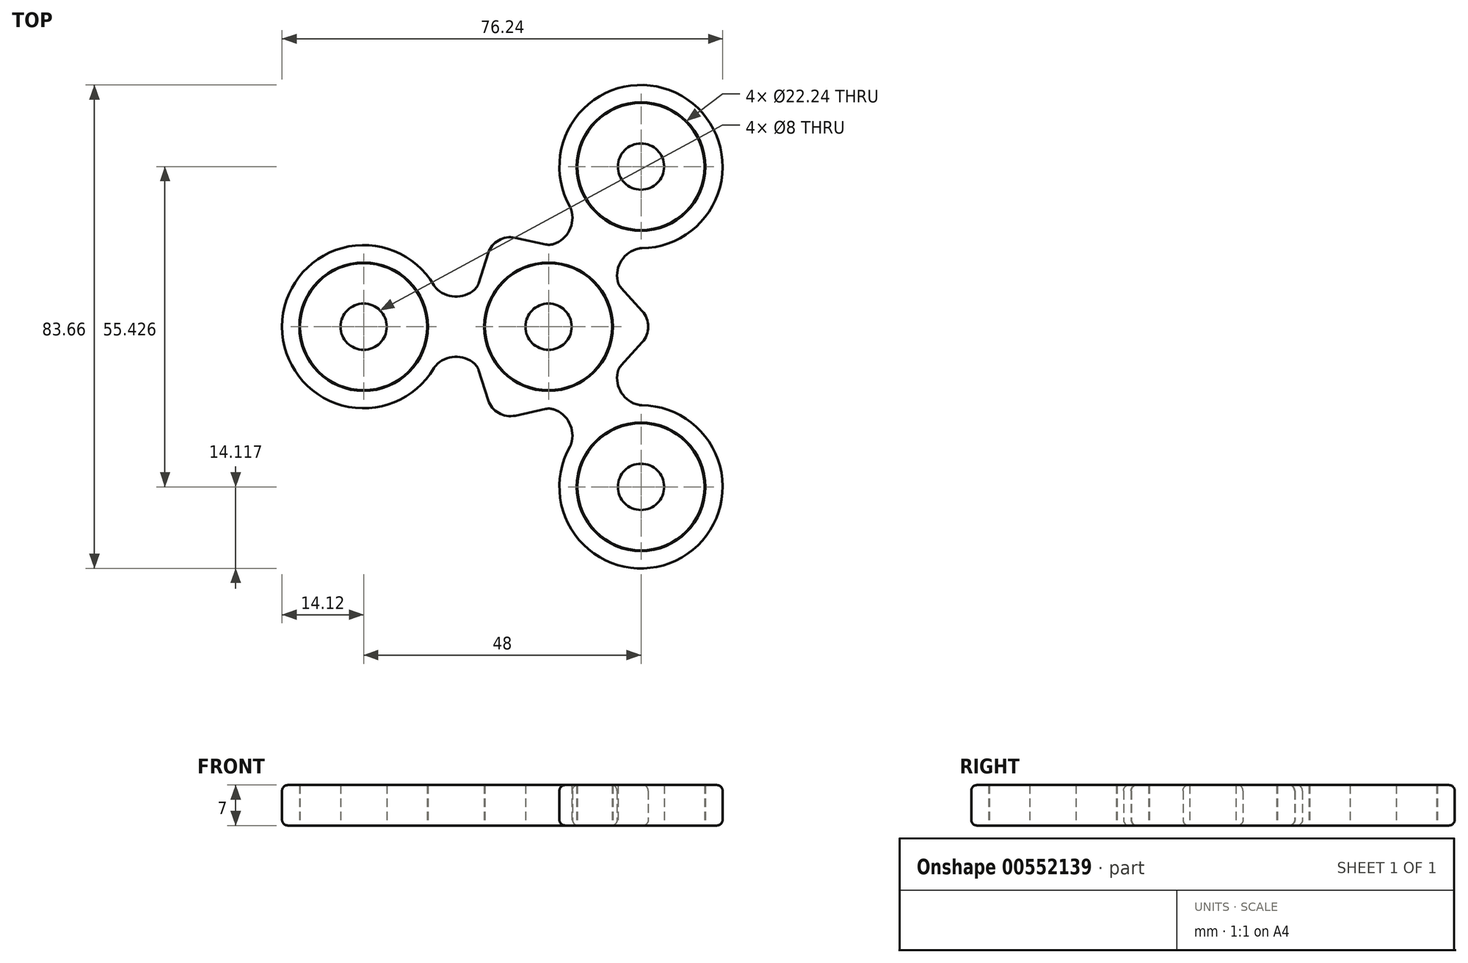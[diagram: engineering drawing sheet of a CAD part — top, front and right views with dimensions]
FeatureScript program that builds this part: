
annotation { "Feature Type Name" : "Feature", "Feature Type Description" : "" }
export const myFeature = defineFeature(function(context is Context, id is Id, definition is map)
    precondition{}
    {
        {
            var Q0;
            Q0=qCreatedBy(makeId("Top.planeOp"),FACE);
            var sketch = newSketch(context, id + "F0", { "sketchPlane" : qUnion([Q0])});
            skCircle(sketch, "E0", {"center": v(0, 0) * mm, "radius": 11 * mm});
            skCircle(sketch, "E1", {"center": v(0, 0) * mm, "radius": 4 * mm});
            skSolve(sketch);
        }
        {
            var Q0;
            Q0=makeQuery(id+"F0.imprint","IMPRINT",FACE,{"disambiguationData":[TD([[makeQuery(id+"F0.imprint","IMPRINT",EDGE,{"derivedFrom":sQuery(id+"F0.wireOp",EDGE,"E0")}),1.0]])]});
            extrude(context, id + "F1", {"entities" : qUnion([Q0]), "endBound" : BoundingType.SYMMETRIC, "depth" : 7 * mm, "offsetDistance" : 25.4 * mm});
        }
        {
            var Q0;
            Q0=qCreatedBy(makeId("Top.planeOp"),FACE);
            var sketch = newSketch(context, id + "F2", { "sketchPlane" : qUnion([Q0])});
            skCircle(sketch, "E2", {"center": v(-32, 0) * mm, "radius": 11 * mm});
            skCircle(sketch, "E3", {"center": v(-32, 0) * mm, "radius": 4 * mm});
            skCircle(sketch, "E4.1.0", {"center": v(16, -27.71) * mm, "radius": 11 * mm});
            skCircle(sketch, "E4.1.1", {"center": v(16, -27.71) * mm, "radius": 4 * mm});
            skCircle(sketch, "E4.2.0", {"center": v(16, 27.71) * mm, "radius": 11 * mm});
            skCircle(sketch, "E4.2.1", {"center": v(16, 27.71) * mm, "radius": 4 * mm});
            skPoint(sketch, "E4.center", {"position": v(0, 0) * mm});
            skSolve(sketch);
        }
        {
            var Q0;
            Q0=makeQuery(id+"F2.imprint","IMPRINT",FACE,{"disambiguationData":[TD([[makeQuery(id+"F2.imprint","IMPRINT",EDGE,{"derivedFrom":sQuery(id+"F2.wireOp",EDGE,"E2")}),1.0]])]});
            var Q1;
            Q1=makeQuery(id+"F2.imprint","IMPRINT",FACE,{"disambiguationData":[TD([[makeQuery(id+"F2.imprint","IMPRINT",EDGE,{"derivedFrom":sQuery(id+"F2.wireOp",EDGE,"E4.2.0")}),1.0]])]});
            var Q2;
            Q2=makeQuery(id+"F2.imprint","IMPRINT",FACE,{"disambiguationData":[TD([[makeQuery(id+"F2.imprint","IMPRINT",EDGE,{"derivedFrom":sQuery(id+"F2.wireOp",EDGE,"E4.1.0")}),1.0]])]});
            extrude(context, id + "F3", {"entities" : qUnion([Q0, Q1, Q2]), "endBound" : BoundingType.SYMMETRIC, "depth" : 7 * mm, "offsetDistance" : 25 * mm});
        }
        {
            var Q0;
            Q0=qCreatedBy(makeId("Top.planeOp"),FACE);
            var sketch = newSketch(context, id + "F4", { "sketchPlane" : qUnion([Q0])});
            skCircle(sketch, "E5.0", {"center": v(-32, 0) * mm, "radius": 11.12 * mm});
            skCircle(sketch, "E6.0", {"center": v(-32, 0) * mm, "radius": 14.12 * mm});
            skPoint(sketch, "E7.center", {"position": v(0, 0) * mm});
            skCircle(sketch, "E8", {"center": v(0, 0) * mm, "radius": 14.12 * mm});
            skCircle(sketch, "E9", {"center": v(0, 0) * mm, "radius": 11.12 * mm});
            skLineSegment(sketch, "E10", {"start": v(-12.26, -7) * mm, "end": v(-10.44, -12.7) * mm});
            skLineSegment(sketch, "E11", {"start": v(-5.78, -15.4) * mm, "end": v(0.07, -14.12) * mm});
            skPoint(sketch, "E12.visualSharp", {"position": v(-9.33, -16.17) * mm});
            skArc(sketch, "E12.filletArc", {"start": v(-10.44, -12.7) * mm, "mid": v(-8.63, -14.95) * mm, "end": v(-5.78, -15.4) * mm});
            skLineSegment(sketch, "E13.1.0", {"start": v(12.2, -7.12) * mm, "end": v(16.22, -2.7) * mm});
            skArc(sketch, "E13.1.1", {"start": v(16.22, -2.7) * mm, "mid": v(17.26, 0) * mm, "end": v(16.22, 2.7) * mm});
            skLineSegment(sketch, "E13.1.2", {"start": v(16.22, 2.7) * mm, "end": v(12.2, 7.12) * mm});
            skLineSegment(sketch, "E13.2.0", {"start": v(0.07, 14.12) * mm, "end": v(-5.78, 15.4) * mm});
            skArc(sketch, "E13.2.1", {"start": v(-5.78, 15.4) * mm, "mid": v(-8.63, 14.95) * mm, "end": v(-10.44, 12.7) * mm});
            skLineSegment(sketch, "E13.2.2", {"start": v(-10.44, 12.7) * mm, "end": v(-12.26, 7) * mm});
            skLineSegment(sketch, "E14", {"start": v(-32, 0) * mm, "end": v(0, 0) * mm, "construction": true});
            skArc(sketch, "E15", {"start": v(-19.74, 7) * mm, "mid": v(-16, 5.2) * mm, "end": v(-12.26, 7) * mm});
            skArc(sketch, "E16.MirrorCS", {"start": v(-19.74, -7) * mm, "mid": v(-16, -5.2) * mm, "end": v(-12.26, -7) * mm});
            skArc(sketch, "E17.1.0", {"start": v(3.8, -20.6) * mm, "mid": v(3.5, -16.46) * mm, "end": v(0.07, -14.12) * mm});
            skCircle(sketch, "E17.1.1", {"center": v(16, -27.71) * mm, "radius": 14.12 * mm});
            skCircle(sketch, "E17.1.2", {"center": v(16, -27.71) * mm, "radius": 11.12 * mm});
            skArc(sketch, "E17.1.3", {"start": v(15.93, -13.6) * mm, "mid": v(12.5, -11.26) * mm, "end": v(12.2, -7.12) * mm});
            skLineSegment(sketch, "E17.1.4", {"start": v(16, -27.71) * mm, "end": v(0, 0) * mm, "construction": true});
            skArc(sketch, "E17.2.0", {"start": v(15.93, 13.6) * mm, "mid": v(12.5, 11.26) * mm, "end": v(12.2, 7.12) * mm});
            skCircle(sketch, "E17.2.1", {"center": v(16, 27.71) * mm, "radius": 14.12 * mm});
            skCircle(sketch, "E17.2.2", {"center": v(16, 27.71) * mm, "radius": 11.12 * mm});
            skArc(sketch, "E17.2.3", {"start": v(3.8, 20.6) * mm, "mid": v(3.5, 16.46) * mm, "end": v(0.07, 14.12) * mm});
            skLineSegment(sketch, "E17.2.4", {"start": v(16, 27.71) * mm, "end": v(0, 0) * mm, "construction": true});
            skSolve(sketch);
        }
        {
            var Q0;
            Q0=makeQuery(id+"F4.imprint","IMPRINT",FACE,{"disambiguationData":[TD([[makeQuery(id+"F4.imprint","IMPRINT",EDGE,{"derivedFrom":sQuery(id+"F4.wireOp",EDGE,"E5.0")}),-1.0]])]});
            var Q1;
            {var subQ0=sQuery(id+"F4.wireOp",EDGE,"gArRicI1-MkRc-wUEB-PXOf-4bWENSXwJS3J");Q1=makeQuery(id+"F4.imprint","IMPRINT",FACE,{"disambiguationData":[TD([[makeQuery(id+"F4.imprint","IMPRINT",EDGE,{"derivedFrom":subQ0}),-1.0]])]});}
            var Q2;
            {var subQ0=sQuery(id+"F4.wireOp",EDGE,"E7.2.2");Q2=makeQuery(id+"F4.imprint","IMPRINT",FACE,{"disambiguationData":[TD([[makeQuery(id+"F4.imprint","IMPRINT",EDGE,{"derivedFrom":subQ0}),-1.0]])]});}
            var Q3;
            Q3=makeQuery(id+"F4.imprint","IMPRINT",FACE,{"disambiguationData":[TD([[makeQuery(id+"F4.imprint","IMPRINT",EDGE,{"derivedFrom":sQuery(id+"F4.wireOp",EDGE,"E7.2.1")}),-1.0]])]});
            var Q4;
            {var subQ0=sQuery(id+"F4.wireOp",EDGE,"E7.1.2");Q4=makeQuery(id+"F4.imprint","IMPRINT",FACE,{"disambiguationData":[TD([[makeQuery(id+"F4.imprint","IMPRINT",EDGE,{"derivedFrom":subQ0}),-1.0]])]});}
            var Q5;
            Q5=makeQuery(id+"F4.imprint","IMPRINT",FACE,{"disambiguationData":[TD([[makeQuery(id+"F4.imprint","IMPRINT",EDGE,{"derivedFrom":sQuery(id+"F4.wireOp",EDGE,"E7.1.1")}),-1.0]])]});
            var Q6;
            Q6=makeQuery(id+"F4.imprint","IMPRINT",FACE,{"disambiguationData":[TD([[makeQuery(id+"F4.imprint","IMPRINT",EDGE,{"derivedFrom":sQuery(id+"F4.wireOp",EDGE,"T5eTbelr-j5SR-9AlQ-x1VE-5ucUHFY7ANY2")}),-1.0]])]});
            var Q7;
            Q7=makeQuery(id+"F4.imprint","IMPRINT",FACE,{"disambiguationData":[TD([[makeQuery(id+"F4.imprint","IMPRINT",EDGE,{"derivedFrom":sQuery(id+"F4.wireOp",EDGE,"E9")}),-1.0]])]});
            var Q8;
            {var subQ0=sQuery(id+"F4.wireOp",EDGE,"E8");var subQ1=sQuery(id+"F4.wireOp",EDGE,"E7.2.0");var subQ2=makeQuery(id+"F4.imprint","INTERSECT",VERTEX,{"disambiguationData":[OD(0.0)],"derivedFrom":[subQ1,subQ0]});Q8=makeQuery(id+"F4.imprint","IMPRINT",FACE,{"disambiguationData":[TD([[makeQuery(id+"F4.imprint","IMPRINT",EDGE,{"disambiguationData":[TD([[subQ2,1.0]])],"derivedFrom":subQ1}),1.0]])]});}
            var Q9;
            {var subQ0=sQuery(id+"F4.wireOp",EDGE,"E7.2.4");Q9=makeQuery(id+"F4.imprint","IMPRINT",FACE,{"disambiguationData":[TD([[makeQuery(id+"F4.imprint","IMPRINT",EDGE,{"derivedFrom":subQ0}),1.0]])]});}
            var Q10;
            {var subQ0=sQuery(id+"F4.wireOp",EDGE,"E8");var subQ1=sQuery(id+"F4.wireOp",EDGE,"E6.0");var subQ2=makeQuery(id+"F4.imprint","INTERSECT",VERTEX,{"disambiguationData":[OD(0.0)],"derivedFrom":[subQ1,subQ0]});Q10=makeQuery(id+"F4.imprint","IMPRINT",FACE,{"disambiguationData":[TD([[makeQuery(id+"F4.imprint","IMPRINT",EDGE,{"disambiguationData":[TD([[subQ2,1.0]])],"derivedFrom":subQ1}),1.0]])]});}
            var Q11;
            {var subQ0=sQuery(id+"F4.wireOp",EDGE,"8a5024f6-34da-4b4a-a497-6fec5d8cf57b0.MirrorCS");Q11=makeQuery(id+"F4.imprint","IMPRINT",FACE,{"disambiguationData":[TD([[makeQuery(id+"F4.imprint","IMPRINT",EDGE,{"derivedFrom":subQ0}),1.0]])]});}
            var Q12;
            {var subQ0=sQuery(id+"F4.wireOp",EDGE,"E8");var subQ1=sQuery(id+"F4.wireOp",EDGE,"E7.1.0");var subQ2=makeQuery(id+"F4.imprint","INTERSECT",VERTEX,{"disambiguationData":[OD(0.0)],"derivedFrom":[subQ1,subQ0]});Q12=makeQuery(id+"F4.imprint","IMPRINT",FACE,{"disambiguationData":[TD([[makeQuery(id+"F4.imprint","IMPRINT",EDGE,{"disambiguationData":[TD([[subQ2,1.0]])],"derivedFrom":subQ1}),1.0]])]});}
            var Q13;
            {var subQ0=sQuery(id+"F4.wireOp",EDGE,"E7.1.4");Q13=makeQuery(id+"F4.imprint","IMPRINT",FACE,{"disambiguationData":[TD([[makeQuery(id+"F4.imprint","IMPRINT",EDGE,{"derivedFrom":subQ0}),1.0]])]});}
            var Q14;
            {var subQ2=sQuery(id+"F4.wireOp",EDGE,"E13.2.0");Q14=makeQuery(id+"F4.imprint","IMPRINT",FACE,{"disambiguationData":[TD([[makeQuery(id+"F4.imprint","IMPRINT",EDGE,{"derivedFrom":subQ2}),1.0]])]});}
            var Q15;
            {var subQ0=sQuery(id+"F4.wireOp",EDGE,"E10");Q15=makeQuery(id+"F4.imprint","IMPRINT",FACE,{"disambiguationData":[TD([[makeQuery(id+"F4.imprint","IMPRINT",EDGE,{"derivedFrom":subQ0}),1.0]])]});}
            var Q16;
            {var subQ0=sQuery(id+"F4.wireOp",EDGE,"E13.1.0");Q16=makeQuery(id+"F4.imprint","IMPRINT",FACE,{"disambiguationData":[TD([[makeQuery(id+"F4.imprint","IMPRINT",EDGE,{"derivedFrom":subQ0}),1.0]])]});}
            var Q17;
            {var subQ0=sQuery(id+"F4.wireOp",EDGE,"E15");Q17=makeQuery(id+"F4.imprint","IMPRINT",FACE,{"disambiguationData":[TD([[makeQuery(id+"F4.imprint","IMPRINT",EDGE,{"derivedFrom":subQ0}),-1.0]])]});}
            var Q18;
            {var subQ0=sQuery(id+"F4.wireOp",EDGE,"E17.2.0");Q18=makeQuery(id+"F4.imprint","IMPRINT",FACE,{"disambiguationData":[TD([[makeQuery(id+"F4.imprint","IMPRINT",EDGE,{"derivedFrom":subQ0}),-1.0]])]});}
            var Q19;
            Q19=makeQuery(id+"F4.imprint","IMPRINT",FACE,{"disambiguationData":[TD([[makeQuery(id+"F4.imprint","IMPRINT",EDGE,{"derivedFrom":sQuery(id+"F4.wireOp",EDGE,"E17.2.2")}),-1.0]])]});
            var Q20;
            {var subQ0=sQuery(id+"F4.wireOp",EDGE,"E17.1.0");Q20=makeQuery(id+"F4.imprint","IMPRINT",FACE,{"disambiguationData":[TD([[makeQuery(id+"F4.imprint","IMPRINT",EDGE,{"derivedFrom":subQ0}),-1.0]])]});}
            var Q21;
            Q21=makeQuery(id+"F4.imprint","IMPRINT",FACE,{"disambiguationData":[TD([[makeQuery(id+"F4.imprint","IMPRINT",EDGE,{"derivedFrom":sQuery(id+"F4.wireOp",EDGE,"E17.1.2")}),-1.0]])]});
            extrude(context, id + "F5", {"entities" : qUnion([Q0, Q1, Q2, Q3, Q4, Q5, Q6, Q7, Q8, Q9, Q10, Q11, Q12, Q13, Q14, Q15, Q16, Q17, Q18, Q19, Q20, Q21]), "endBound" : BoundingType.SYMMETRIC, "depth" : 7 * mm, "offsetDistance" : 25 * mm});
        }
        {
            var Q0;
            Q0=makeQuery(id+"F5.opExtrude","SWEPT_EDGE",EDGE,{"disambiguationData":[OSD([sQuery(id+"F4.wireOp",EDGE,"E7.2.0"),sQuery(id+"F4.wireOp",EDGE,"E7.2.2")])]});
            var Q1;
            Q1=makeQuery(id+"F5.opExtrude","SWEPT_EDGE",EDGE,{"disambiguationData":[OSD([sQuery(id+"F4.wireOp",EDGE,"E7.2.2"),sQuery(id+"F4.wireOp",EDGE,"E8")])]});
            var Q2;
            Q2=makeQuery(id+"F5.opExtrude","SWEPT_EDGE",EDGE,{"disambiguationData":[OSD([sQuery(id+"F4.wireOp",EDGE,"E7.1.4"),sQuery(id+"F4.wireOp",EDGE,"E8")])]});
            var Q3;
            Q3=makeQuery(id+"F5.opExtrude","SWEPT_EDGE",EDGE,{"disambiguationData":[OSD([sQuery(id+"F4.wireOp",EDGE,"E7.1.0"),sQuery(id+"F4.wireOp",EDGE,"E7.1.4")])]});
            var Q4;
            Q4=makeQuery(id+"F5.opExtrude","SWEPT_EDGE",EDGE,{"disambiguationData":[OSD([sQuery(id+"F4.wireOp",EDGE,"E7.2.4"),sQuery(id+"F4.wireOp",EDGE,"E8")])]});
            var Q5;
            Q5=makeQuery(id+"F5.opExtrude","SWEPT_EDGE",EDGE,{"disambiguationData":[OSD([sQuery(id+"F4.wireOp",EDGE,"E7.2.0"),sQuery(id+"F4.wireOp",EDGE,"E7.2.4")])]});
            var Q6;
            Q6=makeQuery(id+"F5.opExtrude","SWEPT_EDGE",EDGE,{"disambiguationData":[OSD([sQuery(id+"F4.wireOp",EDGE,"gArRicI1-MkRc-wUEB-PXOf-4bWENSXwJS3J"),sQuery(id+"F4.wireOp",EDGE,"E8")])]});
            var Q7;
            Q7=makeQuery(id+"F5.opExtrude","SWEPT_EDGE",EDGE,{"disambiguationData":[OSD([sQuery(id+"F4.wireOp",EDGE,"E6.0"),sQuery(id+"F4.wireOp",EDGE,"gArRicI1-MkRc-wUEB-PXOf-4bWENSXwJS3J")])]});
            var Q8;
            Q8=makeQuery(id+"F5.opExtrude","SWEPT_EDGE",EDGE,{"disambiguationData":[OSD([sQuery(id+"F4.wireOp",EDGE,"E6.0"),sQuery(id+"F4.wireOp",EDGE,"8a5024f6-34da-4b4a-a497-6fec5d8cf57b0.MirrorCS")])]});
            var Q9;
            Q9=makeQuery(id+"F5.opExtrude","SWEPT_EDGE",EDGE,{"disambiguationData":[OSD([sQuery(id+"F4.wireOp",EDGE,"8a5024f6-34da-4b4a-a497-6fec5d8cf57b0.MirrorCS"),sQuery(id+"F4.wireOp",EDGE,"E8")])]});
            var Q10;
            Q10=makeQuery(id+"F5.opExtrude","SWEPT_EDGE",EDGE,{"disambiguationData":[OSD([sQuery(id+"F4.wireOp",EDGE,"E7.1.2"),sQuery(id+"F4.wireOp",EDGE,"E8")])]});
            var Q11;
            Q11=makeQuery(id+"F5.opExtrude","SWEPT_EDGE",EDGE,{"disambiguationData":[OSD([sQuery(id+"F4.wireOp",EDGE,"E7.1.0"),sQuery(id+"F4.wireOp",EDGE,"E7.1.2")])]});
            var Q12;
            Q12=makeQuery(id+"F5.opExtrude","SWEPT_EDGE",EDGE,{"disambiguationData":[OSD([sQuery(id+"F4.wireOp",EDGE,"E17.1.0"),sQuery(id+"F4.wireOp",EDGE,"E17.1.1")])]});
            var Q13;
            Q13=makeQuery(id+"F5.opExtrude","SWEPT_EDGE",EDGE,{"disambiguationData":[OSD([sQuery(id+"F4.wireOp",EDGE,"E17.1.1"),sQuery(id+"F4.wireOp",EDGE,"E17.1.3")])]});
            var Q14;
            Q14=makeQuery(id+"F5.opExtrude","SWEPT_EDGE",EDGE,{"disambiguationData":[OSD([sQuery(id+"F4.wireOp",EDGE,"E17.2.0"),sQuery(id+"F4.wireOp",EDGE,"E17.2.1")])]});
            var Q15;
            Q15=makeQuery(id+"F5.opExtrude","SWEPT_EDGE",EDGE,{"disambiguationData":[OSD([sQuery(id+"F4.wireOp",EDGE,"E17.2.1"),sQuery(id+"F4.wireOp",EDGE,"E17.2.3")])]});
            fillet(context, id + "F6", {"entities" : qUnion([Q0, Q1, Q2, Q3, Q4, Q5, Q6, Q7, Q8, Q9, Q10, Q11, Q12, Q13, Q14, Q15]), "radius" : 2.5 * mm, "tangentPropagation" : true, "allowEdgeOverflow" : false});
        }
        {
            var Q0;
            Q0=makeQuery(id+"F5.opExtrude","CAP_EDGE",EDGE,{"disambiguationData":[OSD([sQuery(id+"F4.wireOp",EDGE,"E7.1.0")])],"isStart":true});
            var Q1;
            {var subQ0=sQuery(id+"F4.wireOp",EDGE,"E7.1.2");var subQ1=sQuery(id+"F4.wireOp",EDGE,"E7.1.0");Q1=makeQuery(id+"F6.opFillet","BLEND_EDGE",EDGE,{"blendedFrom":[makeQuery(id+"F5.opExtrude","SWEPT_EDGE",EDGE,{"disambiguationData":[OSD([subQ1,subQ0])]}),makeQuery(id+"F5.opExtrude","CAP_FACE",FACE,{"disambiguationData":[OSD([sQuery(id+"F4.wireOp",EDGE,"E5.0"),sQuery(id+"F4.wireOp",EDGE,"E6.0"),sQuery(id+"F4.wireOp",EDGE,"gArRicI1-MkRc-wUEB-PXOf-4bWENSXwJS3J"),sQuery(id+"F4.wireOp",EDGE,"8a5024f6-34da-4b4a-a497-6fec5d8cf57b0.MirrorCS"),subQ1,sQuery(id+"F4.wireOp",EDGE,"E7.1.1"),subQ0,sQuery(id+"F4.wireOp",EDGE,"E7.1.4"),sQuery(id+"F4.wireOp",EDGE,"E7.2.0"),sQuery(id+"F4.wireOp",EDGE,"E7.2.1"),sQuery(id+"F4.wireOp",EDGE,"E7.2.2"),sQuery(id+"F4.wireOp",EDGE,"E7.2.4"),sQuery(id+"F4.wireOp",EDGE,"E8"),sQuery(id+"F4.wireOp",EDGE,"E9")])],"isStart":true})],"blendedInto":[makeQuery(id+"F5.opExtrude","CAP_FACE",FACE,{"disambiguationData":[OSD([sQuery(id+"F4.wireOp",EDGE,"E5.0"),sQuery(id+"F4.wireOp",EDGE,"E6.0"),sQuery(id+"F4.wireOp",EDGE,"gArRicI1-MkRc-wUEB-PXOf-4bWENSXwJS3J"),sQuery(id+"F4.wireOp",EDGE,"8a5024f6-34da-4b4a-a497-6fec5d8cf57b0.MirrorCS"),subQ1,sQuery(id+"F4.wireOp",EDGE,"E7.1.1"),subQ0,sQuery(id+"F4.wireOp",EDGE,"E7.1.4"),sQuery(id+"F4.wireOp",EDGE,"E7.2.0"),sQuery(id+"F4.wireOp",EDGE,"E7.2.1"),sQuery(id+"F4.wireOp",EDGE,"E7.2.2"),sQuery(id+"F4.wireOp",EDGE,"E7.2.4"),sQuery(id+"F4.wireOp",EDGE,"E8"),sQuery(id+"F4.wireOp",EDGE,"E9")])],"isStart":true})]});}
            var Q2;
            Q2=makeQuery(id+"F5.opExtrude","CAP_EDGE",EDGE,{"disambiguationData":[OSD([sQuery(id+"F4.wireOp",EDGE,"E7.1.2")])],"isStart":true});
            var Q3;
            {var subQ0=sQuery(id+"F4.wireOp",EDGE,"E8");var subQ1=sQuery(id+"F4.wireOp",EDGE,"E7.1.2");Q3=makeQuery(id+"F6.opFillet","BLEND_EDGE",EDGE,{"blendedFrom":[makeQuery(id+"F5.opExtrude","SWEPT_EDGE",EDGE,{"disambiguationData":[OSD([subQ1,subQ0])]}),makeQuery(id+"F5.opExtrude","CAP_FACE",FACE,{"disambiguationData":[OSD([sQuery(id+"F4.wireOp",EDGE,"E5.0"),sQuery(id+"F4.wireOp",EDGE,"E6.0"),sQuery(id+"F4.wireOp",EDGE,"gArRicI1-MkRc-wUEB-PXOf-4bWENSXwJS3J"),sQuery(id+"F4.wireOp",EDGE,"8a5024f6-34da-4b4a-a497-6fec5d8cf57b0.MirrorCS"),sQuery(id+"F4.wireOp",EDGE,"E7.1.0"),sQuery(id+"F4.wireOp",EDGE,"E7.1.1"),subQ1,sQuery(id+"F4.wireOp",EDGE,"E7.1.4"),sQuery(id+"F4.wireOp",EDGE,"E7.2.0"),sQuery(id+"F4.wireOp",EDGE,"E7.2.1"),sQuery(id+"F4.wireOp",EDGE,"E7.2.2"),sQuery(id+"F4.wireOp",EDGE,"E7.2.4"),subQ0,sQuery(id+"F4.wireOp",EDGE,"E9")])],"isStart":true})],"blendedInto":[makeQuery(id+"F5.opExtrude","CAP_FACE",FACE,{"disambiguationData":[OSD([sQuery(id+"F4.wireOp",EDGE,"E5.0"),sQuery(id+"F4.wireOp",EDGE,"E6.0"),sQuery(id+"F4.wireOp",EDGE,"gArRicI1-MkRc-wUEB-PXOf-4bWENSXwJS3J"),sQuery(id+"F4.wireOp",EDGE,"8a5024f6-34da-4b4a-a497-6fec5d8cf57b0.MirrorCS"),sQuery(id+"F4.wireOp",EDGE,"E7.1.0"),sQuery(id+"F4.wireOp",EDGE,"E7.1.1"),subQ1,sQuery(id+"F4.wireOp",EDGE,"E7.1.4"),sQuery(id+"F4.wireOp",EDGE,"E7.2.0"),sQuery(id+"F4.wireOp",EDGE,"E7.2.1"),sQuery(id+"F4.wireOp",EDGE,"E7.2.2"),sQuery(id+"F4.wireOp",EDGE,"E7.2.4"),subQ0,sQuery(id+"F4.wireOp",EDGE,"E9")])],"isStart":true})]});}
            var Q4;
            {var subQ0=sQuery(id+"F4.wireOp",EDGE,"E8");Q4=makeQuery(id+"F5.opExtrude","CAP_EDGE",EDGE,{"disambiguationData":[OSD([subQ0]),TDD([makeQuery(id+"F4.imprint","IMPRINT",EDGE,{"disambiguationData":[TD([[makeQuery(id+"F4.imprint","INTERSECT",VERTEX,{"derivedFrom":[sQuery(id+"F4.wireOp",EDGE,"8a5024f6-34da-4b4a-a497-6fec5d8cf57b0.MirrorCS"),subQ0]}),-1.0]])],"derivedFrom":subQ0})])],"isStart":true});}
            var Q5;
            {var subQ0=sQuery(id+"F4.wireOp",EDGE,"E8");var subQ1=sQuery(id+"F4.wireOp",EDGE,"8a5024f6-34da-4b4a-a497-6fec5d8cf57b0.MirrorCS");Q5=makeQuery(id+"F6.opFillet","BLEND_EDGE",EDGE,{"blendedFrom":[makeQuery(id+"F5.opExtrude","SWEPT_EDGE",EDGE,{"disambiguationData":[OSD([subQ1,subQ0])]}),makeQuery(id+"F5.opExtrude","CAP_FACE",FACE,{"disambiguationData":[OSD([sQuery(id+"F4.wireOp",EDGE,"E5.0"),sQuery(id+"F4.wireOp",EDGE,"E6.0"),sQuery(id+"F4.wireOp",EDGE,"gArRicI1-MkRc-wUEB-PXOf-4bWENSXwJS3J"),subQ1,sQuery(id+"F4.wireOp",EDGE,"E7.1.0"),sQuery(id+"F4.wireOp",EDGE,"E7.1.1"),sQuery(id+"F4.wireOp",EDGE,"E7.1.2"),sQuery(id+"F4.wireOp",EDGE,"E7.1.4"),sQuery(id+"F4.wireOp",EDGE,"E7.2.0"),sQuery(id+"F4.wireOp",EDGE,"E7.2.1"),sQuery(id+"F4.wireOp",EDGE,"E7.2.2"),sQuery(id+"F4.wireOp",EDGE,"E7.2.4"),subQ0,sQuery(id+"F4.wireOp",EDGE,"E9")])],"isStart":true})],"blendedInto":[makeQuery(id+"F5.opExtrude","CAP_FACE",FACE,{"disambiguationData":[OSD([sQuery(id+"F4.wireOp",EDGE,"E5.0"),sQuery(id+"F4.wireOp",EDGE,"E6.0"),sQuery(id+"F4.wireOp",EDGE,"gArRicI1-MkRc-wUEB-PXOf-4bWENSXwJS3J"),subQ1,sQuery(id+"F4.wireOp",EDGE,"E7.1.0"),sQuery(id+"F4.wireOp",EDGE,"E7.1.1"),sQuery(id+"F4.wireOp",EDGE,"E7.1.2"),sQuery(id+"F4.wireOp",EDGE,"E7.1.4"),sQuery(id+"F4.wireOp",EDGE,"E7.2.0"),sQuery(id+"F4.wireOp",EDGE,"E7.2.1"),sQuery(id+"F4.wireOp",EDGE,"E7.2.2"),sQuery(id+"F4.wireOp",EDGE,"E7.2.4"),subQ0,sQuery(id+"F4.wireOp",EDGE,"E9")])],"isStart":true})]});}
            var Q6;
            Q6=makeQuery(id+"F5.opExtrude","CAP_EDGE",EDGE,{"disambiguationData":[OSD([sQuery(id+"F4.wireOp",EDGE,"8a5024f6-34da-4b4a-a497-6fec5d8cf57b0.MirrorCS")])],"isStart":true});
            var Q7;
            {var subQ0=sQuery(id+"F4.wireOp",EDGE,"8a5024f6-34da-4b4a-a497-6fec5d8cf57b0.MirrorCS");var subQ1=sQuery(id+"F4.wireOp",EDGE,"E6.0");Q7=makeQuery(id+"F6.opFillet","BLEND_EDGE",EDGE,{"blendedFrom":[makeQuery(id+"F5.opExtrude","SWEPT_EDGE",EDGE,{"disambiguationData":[OSD([subQ1,subQ0])]}),makeQuery(id+"F5.opExtrude","CAP_FACE",FACE,{"disambiguationData":[OSD([sQuery(id+"F4.wireOp",EDGE,"E5.0"),subQ1,sQuery(id+"F4.wireOp",EDGE,"gArRicI1-MkRc-wUEB-PXOf-4bWENSXwJS3J"),subQ0,sQuery(id+"F4.wireOp",EDGE,"E7.1.0"),sQuery(id+"F4.wireOp",EDGE,"E7.1.1"),sQuery(id+"F4.wireOp",EDGE,"E7.1.2"),sQuery(id+"F4.wireOp",EDGE,"E7.1.4"),sQuery(id+"F4.wireOp",EDGE,"E7.2.0"),sQuery(id+"F4.wireOp",EDGE,"E7.2.1"),sQuery(id+"F4.wireOp",EDGE,"E7.2.2"),sQuery(id+"F4.wireOp",EDGE,"E7.2.4"),sQuery(id+"F4.wireOp",EDGE,"E8"),sQuery(id+"F4.wireOp",EDGE,"E9")])],"isStart":true})],"blendedInto":[makeQuery(id+"F5.opExtrude","CAP_FACE",FACE,{"disambiguationData":[OSD([sQuery(id+"F4.wireOp",EDGE,"E5.0"),subQ1,sQuery(id+"F4.wireOp",EDGE,"gArRicI1-MkRc-wUEB-PXOf-4bWENSXwJS3J"),subQ0,sQuery(id+"F4.wireOp",EDGE,"E7.1.0"),sQuery(id+"F4.wireOp",EDGE,"E7.1.1"),sQuery(id+"F4.wireOp",EDGE,"E7.1.2"),sQuery(id+"F4.wireOp",EDGE,"E7.1.4"),sQuery(id+"F4.wireOp",EDGE,"E7.2.0"),sQuery(id+"F4.wireOp",EDGE,"E7.2.1"),sQuery(id+"F4.wireOp",EDGE,"E7.2.2"),sQuery(id+"F4.wireOp",EDGE,"E7.2.4"),sQuery(id+"F4.wireOp",EDGE,"E8"),sQuery(id+"F4.wireOp",EDGE,"E9")])],"isStart":true})]});}
            var Q8;
            Q8=makeQuery(id+"F5.opExtrude","CAP_EDGE",EDGE,{"disambiguationData":[OSD([sQuery(id+"F4.wireOp",EDGE,"E6.0")])],"isStart":true});
            var Q9;
            {var subQ0=sQuery(id+"F4.wireOp",EDGE,"gArRicI1-MkRc-wUEB-PXOf-4bWENSXwJS3J");var subQ1=sQuery(id+"F4.wireOp",EDGE,"E6.0");Q9=makeQuery(id+"F6.opFillet","BLEND_EDGE",EDGE,{"blendedFrom":[makeQuery(id+"F5.opExtrude","SWEPT_EDGE",EDGE,{"disambiguationData":[OSD([subQ1,subQ0])]}),makeQuery(id+"F5.opExtrude","CAP_FACE",FACE,{"disambiguationData":[OSD([sQuery(id+"F4.wireOp",EDGE,"E5.0"),subQ1,subQ0,sQuery(id+"F4.wireOp",EDGE,"8a5024f6-34da-4b4a-a497-6fec5d8cf57b0.MirrorCS"),sQuery(id+"F4.wireOp",EDGE,"E7.1.0"),sQuery(id+"F4.wireOp",EDGE,"E7.1.1"),sQuery(id+"F4.wireOp",EDGE,"E7.1.2"),sQuery(id+"F4.wireOp",EDGE,"E7.1.4"),sQuery(id+"F4.wireOp",EDGE,"E7.2.0"),sQuery(id+"F4.wireOp",EDGE,"E7.2.1"),sQuery(id+"F4.wireOp",EDGE,"E7.2.2"),sQuery(id+"F4.wireOp",EDGE,"E7.2.4"),sQuery(id+"F4.wireOp",EDGE,"E8"),sQuery(id+"F4.wireOp",EDGE,"E9")])],"isStart":true})],"blendedInto":[makeQuery(id+"F5.opExtrude","CAP_FACE",FACE,{"disambiguationData":[OSD([sQuery(id+"F4.wireOp",EDGE,"E5.0"),subQ1,subQ0,sQuery(id+"F4.wireOp",EDGE,"8a5024f6-34da-4b4a-a497-6fec5d8cf57b0.MirrorCS"),sQuery(id+"F4.wireOp",EDGE,"E7.1.0"),sQuery(id+"F4.wireOp",EDGE,"E7.1.1"),sQuery(id+"F4.wireOp",EDGE,"E7.1.2"),sQuery(id+"F4.wireOp",EDGE,"E7.1.4"),sQuery(id+"F4.wireOp",EDGE,"E7.2.0"),sQuery(id+"F4.wireOp",EDGE,"E7.2.1"),sQuery(id+"F4.wireOp",EDGE,"E7.2.2"),sQuery(id+"F4.wireOp",EDGE,"E7.2.4"),sQuery(id+"F4.wireOp",EDGE,"E8"),sQuery(id+"F4.wireOp",EDGE,"E9")])],"isStart":true})]});}
            var Q10;
            {var subQ0=sQuery(id+"F4.wireOp",EDGE,"E8");var subQ1=sQuery(id+"F4.wireOp",EDGE,"gArRicI1-MkRc-wUEB-PXOf-4bWENSXwJS3J");Q10=makeQuery(id+"F6.opFillet","BLEND_EDGE",EDGE,{"blendedFrom":[makeQuery(id+"F5.opExtrude","SWEPT_EDGE",EDGE,{"disambiguationData":[OSD([subQ1,subQ0])]}),makeQuery(id+"F5.opExtrude","CAP_FACE",FACE,{"disambiguationData":[OSD([sQuery(id+"F4.wireOp",EDGE,"E5.0"),sQuery(id+"F4.wireOp",EDGE,"E6.0"),subQ1,sQuery(id+"F4.wireOp",EDGE,"8a5024f6-34da-4b4a-a497-6fec5d8cf57b0.MirrorCS"),sQuery(id+"F4.wireOp",EDGE,"E7.1.0"),sQuery(id+"F4.wireOp",EDGE,"E7.1.1"),sQuery(id+"F4.wireOp",EDGE,"E7.1.2"),sQuery(id+"F4.wireOp",EDGE,"E7.1.4"),sQuery(id+"F4.wireOp",EDGE,"E7.2.0"),sQuery(id+"F4.wireOp",EDGE,"E7.2.1"),sQuery(id+"F4.wireOp",EDGE,"E7.2.2"),sQuery(id+"F4.wireOp",EDGE,"E7.2.4"),subQ0,sQuery(id+"F4.wireOp",EDGE,"E9")])],"isStart":true})],"blendedInto":[makeQuery(id+"F5.opExtrude","CAP_FACE",FACE,{"disambiguationData":[OSD([sQuery(id+"F4.wireOp",EDGE,"E5.0"),sQuery(id+"F4.wireOp",EDGE,"E6.0"),subQ1,sQuery(id+"F4.wireOp",EDGE,"8a5024f6-34da-4b4a-a497-6fec5d8cf57b0.MirrorCS"),sQuery(id+"F4.wireOp",EDGE,"E7.1.0"),sQuery(id+"F4.wireOp",EDGE,"E7.1.1"),sQuery(id+"F4.wireOp",EDGE,"E7.1.2"),sQuery(id+"F4.wireOp",EDGE,"E7.1.4"),sQuery(id+"F4.wireOp",EDGE,"E7.2.0"),sQuery(id+"F4.wireOp",EDGE,"E7.2.1"),sQuery(id+"F4.wireOp",EDGE,"E7.2.2"),sQuery(id+"F4.wireOp",EDGE,"E7.2.4"),subQ0,sQuery(id+"F4.wireOp",EDGE,"E9")])],"isStart":true})]});}
            var Q11;
            {var subQ0=sQuery(id+"F4.wireOp",EDGE,"E8");Q11=makeQuery(id+"F5.opExtrude","CAP_EDGE",EDGE,{"disambiguationData":[OSD([subQ0]),TDD([makeQuery(id+"F4.imprint","IMPRINT",EDGE,{"disambiguationData":[TD([[makeQuery(id+"F4.imprint","INTERSECT",VERTEX,{"derivedFrom":[sQuery(id+"F4.wireOp",EDGE,"gArRicI1-MkRc-wUEB-PXOf-4bWENSXwJS3J"),subQ0]}),1.0]])],"derivedFrom":subQ0})])],"isStart":true});}
            var Q12;
            {var subQ0=sQuery(id+"F4.wireOp",EDGE,"E8");var subQ1=sQuery(id+"F4.wireOp",EDGE,"E7.2.4");Q12=makeQuery(id+"F6.opFillet","BLEND_EDGE",EDGE,{"blendedFrom":[makeQuery(id+"F5.opExtrude","SWEPT_EDGE",EDGE,{"disambiguationData":[OSD([subQ1,subQ0])]}),makeQuery(id+"F5.opExtrude","CAP_FACE",FACE,{"disambiguationData":[OSD([sQuery(id+"F4.wireOp",EDGE,"E5.0"),sQuery(id+"F4.wireOp",EDGE,"E6.0"),sQuery(id+"F4.wireOp",EDGE,"gArRicI1-MkRc-wUEB-PXOf-4bWENSXwJS3J"),sQuery(id+"F4.wireOp",EDGE,"8a5024f6-34da-4b4a-a497-6fec5d8cf57b0.MirrorCS"),sQuery(id+"F4.wireOp",EDGE,"E7.1.0"),sQuery(id+"F4.wireOp",EDGE,"E7.1.1"),sQuery(id+"F4.wireOp",EDGE,"E7.1.2"),sQuery(id+"F4.wireOp",EDGE,"E7.1.4"),sQuery(id+"F4.wireOp",EDGE,"E7.2.0"),sQuery(id+"F4.wireOp",EDGE,"E7.2.1"),sQuery(id+"F4.wireOp",EDGE,"E7.2.2"),subQ1,subQ0,sQuery(id+"F4.wireOp",EDGE,"E9")])],"isStart":true})],"blendedInto":[makeQuery(id+"F5.opExtrude","CAP_FACE",FACE,{"disambiguationData":[OSD([sQuery(id+"F4.wireOp",EDGE,"E5.0"),sQuery(id+"F4.wireOp",EDGE,"E6.0"),sQuery(id+"F4.wireOp",EDGE,"gArRicI1-MkRc-wUEB-PXOf-4bWENSXwJS3J"),sQuery(id+"F4.wireOp",EDGE,"8a5024f6-34da-4b4a-a497-6fec5d8cf57b0.MirrorCS"),sQuery(id+"F4.wireOp",EDGE,"E7.1.0"),sQuery(id+"F4.wireOp",EDGE,"E7.1.1"),sQuery(id+"F4.wireOp",EDGE,"E7.1.2"),sQuery(id+"F4.wireOp",EDGE,"E7.1.4"),sQuery(id+"F4.wireOp",EDGE,"E7.2.0"),sQuery(id+"F4.wireOp",EDGE,"E7.2.1"),sQuery(id+"F4.wireOp",EDGE,"E7.2.2"),subQ1,subQ0,sQuery(id+"F4.wireOp",EDGE,"E9")])],"isStart":true})]});}
            var Q13;
            Q13=makeQuery(id+"F5.opExtrude","CAP_EDGE",EDGE,{"disambiguationData":[OSD([sQuery(id+"F4.wireOp",EDGE,"E7.2.4")])],"isStart":true});
            var Q14;
            {var subQ0=sQuery(id+"F4.wireOp",EDGE,"E7.2.4");var subQ1=sQuery(id+"F4.wireOp",EDGE,"E7.2.0");Q14=makeQuery(id+"F6.opFillet","BLEND_EDGE",EDGE,{"blendedFrom":[makeQuery(id+"F5.opExtrude","SWEPT_EDGE",EDGE,{"disambiguationData":[OSD([subQ1,subQ0])]}),makeQuery(id+"F5.opExtrude","CAP_FACE",FACE,{"disambiguationData":[OSD([sQuery(id+"F4.wireOp",EDGE,"E5.0"),sQuery(id+"F4.wireOp",EDGE,"E6.0"),sQuery(id+"F4.wireOp",EDGE,"gArRicI1-MkRc-wUEB-PXOf-4bWENSXwJS3J"),sQuery(id+"F4.wireOp",EDGE,"8a5024f6-34da-4b4a-a497-6fec5d8cf57b0.MirrorCS"),sQuery(id+"F4.wireOp",EDGE,"E7.1.0"),sQuery(id+"F4.wireOp",EDGE,"E7.1.1"),sQuery(id+"F4.wireOp",EDGE,"E7.1.2"),sQuery(id+"F4.wireOp",EDGE,"E7.1.4"),subQ1,sQuery(id+"F4.wireOp",EDGE,"E7.2.1"),sQuery(id+"F4.wireOp",EDGE,"E7.2.2"),subQ0,sQuery(id+"F4.wireOp",EDGE,"E8"),sQuery(id+"F4.wireOp",EDGE,"E9")])],"isStart":true})],"blendedInto":[makeQuery(id+"F5.opExtrude","CAP_FACE",FACE,{"disambiguationData":[OSD([sQuery(id+"F4.wireOp",EDGE,"E5.0"),sQuery(id+"F4.wireOp",EDGE,"E6.0"),sQuery(id+"F4.wireOp",EDGE,"gArRicI1-MkRc-wUEB-PXOf-4bWENSXwJS3J"),sQuery(id+"F4.wireOp",EDGE,"8a5024f6-34da-4b4a-a497-6fec5d8cf57b0.MirrorCS"),sQuery(id+"F4.wireOp",EDGE,"E7.1.0"),sQuery(id+"F4.wireOp",EDGE,"E7.1.1"),sQuery(id+"F4.wireOp",EDGE,"E7.1.2"),sQuery(id+"F4.wireOp",EDGE,"E7.1.4"),subQ1,sQuery(id+"F4.wireOp",EDGE,"E7.2.1"),sQuery(id+"F4.wireOp",EDGE,"E7.2.2"),subQ0,sQuery(id+"F4.wireOp",EDGE,"E8"),sQuery(id+"F4.wireOp",EDGE,"E9")])],"isStart":true})]});}
            var Q15;
            Q15=makeQuery(id+"F5.opExtrude","CAP_EDGE",EDGE,{"disambiguationData":[OSD([sQuery(id+"F4.wireOp",EDGE,"gArRicI1-MkRc-wUEB-PXOf-4bWENSXwJS3J")])],"isStart":true});
            var Q16;
            Q16=makeQuery(id+"F5.opExtrude","CAP_EDGE",EDGE,{"disambiguationData":[OSD([sQuery(id+"F4.wireOp",EDGE,"E7.2.0")])],"isStart":true});
            var Q17;
            {var subQ0=sQuery(id+"F4.wireOp",EDGE,"E7.2.2");var subQ1=sQuery(id+"F4.wireOp",EDGE,"E7.2.0");Q17=makeQuery(id+"F6.opFillet","BLEND_EDGE",EDGE,{"blendedFrom":[makeQuery(id+"F5.opExtrude","SWEPT_EDGE",EDGE,{"disambiguationData":[OSD([subQ1,subQ0])]}),makeQuery(id+"F5.opExtrude","CAP_FACE",FACE,{"disambiguationData":[OSD([sQuery(id+"F4.wireOp",EDGE,"E5.0"),sQuery(id+"F4.wireOp",EDGE,"E6.0"),sQuery(id+"F4.wireOp",EDGE,"gArRicI1-MkRc-wUEB-PXOf-4bWENSXwJS3J"),sQuery(id+"F4.wireOp",EDGE,"8a5024f6-34da-4b4a-a497-6fec5d8cf57b0.MirrorCS"),sQuery(id+"F4.wireOp",EDGE,"E7.1.0"),sQuery(id+"F4.wireOp",EDGE,"E7.1.1"),sQuery(id+"F4.wireOp",EDGE,"E7.1.2"),sQuery(id+"F4.wireOp",EDGE,"E7.1.4"),subQ1,sQuery(id+"F4.wireOp",EDGE,"E7.2.1"),subQ0,sQuery(id+"F4.wireOp",EDGE,"E7.2.4"),sQuery(id+"F4.wireOp",EDGE,"E8"),sQuery(id+"F4.wireOp",EDGE,"E9")])],"isStart":true})],"blendedInto":[makeQuery(id+"F5.opExtrude","CAP_FACE",FACE,{"disambiguationData":[OSD([sQuery(id+"F4.wireOp",EDGE,"E5.0"),sQuery(id+"F4.wireOp",EDGE,"E6.0"),sQuery(id+"F4.wireOp",EDGE,"gArRicI1-MkRc-wUEB-PXOf-4bWENSXwJS3J"),sQuery(id+"F4.wireOp",EDGE,"8a5024f6-34da-4b4a-a497-6fec5d8cf57b0.MirrorCS"),sQuery(id+"F4.wireOp",EDGE,"E7.1.0"),sQuery(id+"F4.wireOp",EDGE,"E7.1.1"),sQuery(id+"F4.wireOp",EDGE,"E7.1.2"),sQuery(id+"F4.wireOp",EDGE,"E7.1.4"),subQ1,sQuery(id+"F4.wireOp",EDGE,"E7.2.1"),subQ0,sQuery(id+"F4.wireOp",EDGE,"E7.2.4"),sQuery(id+"F4.wireOp",EDGE,"E8"),sQuery(id+"F4.wireOp",EDGE,"E9")])],"isStart":true})]});}
            var Q18;
            Q18=makeQuery(id+"F5.opExtrude","CAP_EDGE",EDGE,{"disambiguationData":[OSD([sQuery(id+"F4.wireOp",EDGE,"E7.2.2")])],"isStart":true});
            var Q19;
            {var subQ0=sQuery(id+"F4.wireOp",EDGE,"E8");var subQ1=sQuery(id+"F4.wireOp",EDGE,"E7.2.2");Q19=makeQuery(id+"F6.opFillet","BLEND_EDGE",EDGE,{"blendedFrom":[makeQuery(id+"F5.opExtrude","SWEPT_EDGE",EDGE,{"disambiguationData":[OSD([subQ1,subQ0])]}),makeQuery(id+"F5.opExtrude","CAP_FACE",FACE,{"disambiguationData":[OSD([sQuery(id+"F4.wireOp",EDGE,"E5.0"),sQuery(id+"F4.wireOp",EDGE,"E6.0"),sQuery(id+"F4.wireOp",EDGE,"gArRicI1-MkRc-wUEB-PXOf-4bWENSXwJS3J"),sQuery(id+"F4.wireOp",EDGE,"8a5024f6-34da-4b4a-a497-6fec5d8cf57b0.MirrorCS"),sQuery(id+"F4.wireOp",EDGE,"E7.1.0"),sQuery(id+"F4.wireOp",EDGE,"E7.1.1"),sQuery(id+"F4.wireOp",EDGE,"E7.1.2"),sQuery(id+"F4.wireOp",EDGE,"E7.1.4"),sQuery(id+"F4.wireOp",EDGE,"E7.2.0"),sQuery(id+"F4.wireOp",EDGE,"E7.2.1"),subQ1,sQuery(id+"F4.wireOp",EDGE,"E7.2.4"),subQ0,sQuery(id+"F4.wireOp",EDGE,"E9")])],"isStart":true})],"blendedInto":[makeQuery(id+"F5.opExtrude","CAP_FACE",FACE,{"disambiguationData":[OSD([sQuery(id+"F4.wireOp",EDGE,"E5.0"),sQuery(id+"F4.wireOp",EDGE,"E6.0"),sQuery(id+"F4.wireOp",EDGE,"gArRicI1-MkRc-wUEB-PXOf-4bWENSXwJS3J"),sQuery(id+"F4.wireOp",EDGE,"8a5024f6-34da-4b4a-a497-6fec5d8cf57b0.MirrorCS"),sQuery(id+"F4.wireOp",EDGE,"E7.1.0"),sQuery(id+"F4.wireOp",EDGE,"E7.1.1"),sQuery(id+"F4.wireOp",EDGE,"E7.1.2"),sQuery(id+"F4.wireOp",EDGE,"E7.1.4"),sQuery(id+"F4.wireOp",EDGE,"E7.2.0"),sQuery(id+"F4.wireOp",EDGE,"E7.2.1"),subQ1,sQuery(id+"F4.wireOp",EDGE,"E7.2.4"),subQ0,sQuery(id+"F4.wireOp",EDGE,"E9")])],"isStart":true})]});}
            var Q20;
            {var subQ0=sQuery(id+"F4.wireOp",EDGE,"E8");Q20=makeQuery(id+"F5.opExtrude","CAP_EDGE",EDGE,{"disambiguationData":[OSD([subQ0]),TDD([makeQuery(id+"F4.imprint","IMPRINT",EDGE,{"disambiguationData":[TD([[makeQuery(id+"F4.imprint","INTERSECT",VERTEX,{"derivedFrom":[sQuery(id+"F4.wireOp",EDGE,"E7.1.4"),subQ0]}),-1.0]])],"derivedFrom":subQ0})])],"isStart":true});}
            var Q21;
            {var subQ0=sQuery(id+"F4.wireOp",EDGE,"E8");var subQ1=sQuery(id+"F4.wireOp",EDGE,"E7.1.4");Q21=makeQuery(id+"F6.opFillet","BLEND_EDGE",EDGE,{"blendedFrom":[makeQuery(id+"F5.opExtrude","SWEPT_EDGE",EDGE,{"disambiguationData":[OSD([subQ1,subQ0])]}),makeQuery(id+"F5.opExtrude","CAP_FACE",FACE,{"disambiguationData":[OSD([sQuery(id+"F4.wireOp",EDGE,"E5.0"),sQuery(id+"F4.wireOp",EDGE,"E6.0"),sQuery(id+"F4.wireOp",EDGE,"gArRicI1-MkRc-wUEB-PXOf-4bWENSXwJS3J"),sQuery(id+"F4.wireOp",EDGE,"8a5024f6-34da-4b4a-a497-6fec5d8cf57b0.MirrorCS"),sQuery(id+"F4.wireOp",EDGE,"E7.1.0"),sQuery(id+"F4.wireOp",EDGE,"E7.1.1"),sQuery(id+"F4.wireOp",EDGE,"E7.1.2"),subQ1,sQuery(id+"F4.wireOp",EDGE,"E7.2.0"),sQuery(id+"F4.wireOp",EDGE,"E7.2.1"),sQuery(id+"F4.wireOp",EDGE,"E7.2.2"),sQuery(id+"F4.wireOp",EDGE,"E7.2.4"),subQ0,sQuery(id+"F4.wireOp",EDGE,"E9")])],"isStart":true})],"blendedInto":[makeQuery(id+"F5.opExtrude","CAP_FACE",FACE,{"disambiguationData":[OSD([sQuery(id+"F4.wireOp",EDGE,"E5.0"),sQuery(id+"F4.wireOp",EDGE,"E6.0"),sQuery(id+"F4.wireOp",EDGE,"gArRicI1-MkRc-wUEB-PXOf-4bWENSXwJS3J"),sQuery(id+"F4.wireOp",EDGE,"8a5024f6-34da-4b4a-a497-6fec5d8cf57b0.MirrorCS"),sQuery(id+"F4.wireOp",EDGE,"E7.1.0"),sQuery(id+"F4.wireOp",EDGE,"E7.1.1"),sQuery(id+"F4.wireOp",EDGE,"E7.1.2"),subQ1,sQuery(id+"F4.wireOp",EDGE,"E7.2.0"),sQuery(id+"F4.wireOp",EDGE,"E7.2.1"),sQuery(id+"F4.wireOp",EDGE,"E7.2.2"),sQuery(id+"F4.wireOp",EDGE,"E7.2.4"),subQ0,sQuery(id+"F4.wireOp",EDGE,"E9")])],"isStart":true})]});}
            var Q22;
            Q22=makeQuery(id+"F5.opExtrude","CAP_EDGE",EDGE,{"disambiguationData":[OSD([sQuery(id+"F4.wireOp",EDGE,"E7.1.4")])],"isStart":true});
            var Q23;
            {var subQ0=sQuery(id+"F4.wireOp",EDGE,"E7.1.4");var subQ1=sQuery(id+"F4.wireOp",EDGE,"E7.1.0");Q23=makeQuery(id+"F6.opFillet","BLEND_EDGE",EDGE,{"blendedFrom":[makeQuery(id+"F5.opExtrude","SWEPT_EDGE",EDGE,{"disambiguationData":[OSD([subQ1,subQ0])]}),makeQuery(id+"F5.opExtrude","CAP_FACE",FACE,{"disambiguationData":[OSD([sQuery(id+"F4.wireOp",EDGE,"E5.0"),sQuery(id+"F4.wireOp",EDGE,"E6.0"),sQuery(id+"F4.wireOp",EDGE,"gArRicI1-MkRc-wUEB-PXOf-4bWENSXwJS3J"),sQuery(id+"F4.wireOp",EDGE,"8a5024f6-34da-4b4a-a497-6fec5d8cf57b0.MirrorCS"),subQ1,sQuery(id+"F4.wireOp",EDGE,"E7.1.1"),sQuery(id+"F4.wireOp",EDGE,"E7.1.2"),subQ0,sQuery(id+"F4.wireOp",EDGE,"E7.2.0"),sQuery(id+"F4.wireOp",EDGE,"E7.2.1"),sQuery(id+"F4.wireOp",EDGE,"E7.2.2"),sQuery(id+"F4.wireOp",EDGE,"E7.2.4"),sQuery(id+"F4.wireOp",EDGE,"E8"),sQuery(id+"F4.wireOp",EDGE,"E9")])],"isStart":true})],"blendedInto":[makeQuery(id+"F5.opExtrude","CAP_FACE",FACE,{"disambiguationData":[OSD([sQuery(id+"F4.wireOp",EDGE,"E5.0"),sQuery(id+"F4.wireOp",EDGE,"E6.0"),sQuery(id+"F4.wireOp",EDGE,"gArRicI1-MkRc-wUEB-PXOf-4bWENSXwJS3J"),sQuery(id+"F4.wireOp",EDGE,"8a5024f6-34da-4b4a-a497-6fec5d8cf57b0.MirrorCS"),subQ1,sQuery(id+"F4.wireOp",EDGE,"E7.1.1"),sQuery(id+"F4.wireOp",EDGE,"E7.1.2"),subQ0,sQuery(id+"F4.wireOp",EDGE,"E7.2.0"),sQuery(id+"F4.wireOp",EDGE,"E7.2.1"),sQuery(id+"F4.wireOp",EDGE,"E7.2.2"),sQuery(id+"F4.wireOp",EDGE,"E7.2.4"),sQuery(id+"F4.wireOp",EDGE,"E8"),sQuery(id+"F4.wireOp",EDGE,"E9")])],"isStart":true})]});}
            var Q24;
            Q24=makeQuery(id+"F5.opExtrude","CAP_EDGE",EDGE,{"disambiguationData":[OSD([sQuery(id+"F4.wireOp",EDGE,"E7.2.2")])],"isStart":false});
            var Q25;
            {var subQ0=sQuery(id+"F4.wireOp",EDGE,"E7.2.2");var subQ1=sQuery(id+"F4.wireOp",EDGE,"E7.2.0");Q25=makeQuery(id+"F6.opFillet","BLEND_EDGE",EDGE,{"blendedFrom":[makeQuery(id+"F5.opExtrude","SWEPT_EDGE",EDGE,{"disambiguationData":[OSD([subQ1,subQ0])]}),makeQuery(id+"F5.opExtrude","CAP_FACE",FACE,{"disambiguationData":[OSD([sQuery(id+"F4.wireOp",EDGE,"E5.0"),sQuery(id+"F4.wireOp",EDGE,"E6.0"),sQuery(id+"F4.wireOp",EDGE,"gArRicI1-MkRc-wUEB-PXOf-4bWENSXwJS3J"),sQuery(id+"F4.wireOp",EDGE,"8a5024f6-34da-4b4a-a497-6fec5d8cf57b0.MirrorCS"),sQuery(id+"F4.wireOp",EDGE,"E7.1.0"),sQuery(id+"F4.wireOp",EDGE,"E7.1.1"),sQuery(id+"F4.wireOp",EDGE,"E7.1.2"),sQuery(id+"F4.wireOp",EDGE,"E7.1.4"),subQ1,sQuery(id+"F4.wireOp",EDGE,"E7.2.1"),subQ0,sQuery(id+"F4.wireOp",EDGE,"E7.2.4"),sQuery(id+"F4.wireOp",EDGE,"E8"),sQuery(id+"F4.wireOp",EDGE,"E9")])],"isStart":false})],"blendedInto":[makeQuery(id+"F5.opExtrude","CAP_FACE",FACE,{"disambiguationData":[OSD([sQuery(id+"F4.wireOp",EDGE,"E5.0"),sQuery(id+"F4.wireOp",EDGE,"E6.0"),sQuery(id+"F4.wireOp",EDGE,"gArRicI1-MkRc-wUEB-PXOf-4bWENSXwJS3J"),sQuery(id+"F4.wireOp",EDGE,"8a5024f6-34da-4b4a-a497-6fec5d8cf57b0.MirrorCS"),sQuery(id+"F4.wireOp",EDGE,"E7.1.0"),sQuery(id+"F4.wireOp",EDGE,"E7.1.1"),sQuery(id+"F4.wireOp",EDGE,"E7.1.2"),sQuery(id+"F4.wireOp",EDGE,"E7.1.4"),subQ1,sQuery(id+"F4.wireOp",EDGE,"E7.2.1"),subQ0,sQuery(id+"F4.wireOp",EDGE,"E7.2.4"),sQuery(id+"F4.wireOp",EDGE,"E8"),sQuery(id+"F4.wireOp",EDGE,"E9")])],"isStart":false})]});}
            var Q26;
            {var subQ0=sQuery(id+"F4.wireOp",EDGE,"E8");var subQ1=sQuery(id+"F4.wireOp",EDGE,"E7.2.2");Q26=makeQuery(id+"F6.opFillet","BLEND_EDGE",EDGE,{"blendedFrom":[makeQuery(id+"F5.opExtrude","SWEPT_EDGE",EDGE,{"disambiguationData":[OSD([subQ1,subQ0])]}),makeQuery(id+"F5.opExtrude","CAP_FACE",FACE,{"disambiguationData":[OSD([sQuery(id+"F4.wireOp",EDGE,"E5.0"),sQuery(id+"F4.wireOp",EDGE,"E6.0"),sQuery(id+"F4.wireOp",EDGE,"gArRicI1-MkRc-wUEB-PXOf-4bWENSXwJS3J"),sQuery(id+"F4.wireOp",EDGE,"8a5024f6-34da-4b4a-a497-6fec5d8cf57b0.MirrorCS"),sQuery(id+"F4.wireOp",EDGE,"E7.1.0"),sQuery(id+"F4.wireOp",EDGE,"E7.1.1"),sQuery(id+"F4.wireOp",EDGE,"E7.1.2"),sQuery(id+"F4.wireOp",EDGE,"E7.1.4"),sQuery(id+"F4.wireOp",EDGE,"E7.2.0"),sQuery(id+"F4.wireOp",EDGE,"E7.2.1"),subQ1,sQuery(id+"F4.wireOp",EDGE,"E7.2.4"),subQ0,sQuery(id+"F4.wireOp",EDGE,"E9")])],"isStart":false})],"blendedInto":[makeQuery(id+"F5.opExtrude","CAP_FACE",FACE,{"disambiguationData":[OSD([sQuery(id+"F4.wireOp",EDGE,"E5.0"),sQuery(id+"F4.wireOp",EDGE,"E6.0"),sQuery(id+"F4.wireOp",EDGE,"gArRicI1-MkRc-wUEB-PXOf-4bWENSXwJS3J"),sQuery(id+"F4.wireOp",EDGE,"8a5024f6-34da-4b4a-a497-6fec5d8cf57b0.MirrorCS"),sQuery(id+"F4.wireOp",EDGE,"E7.1.0"),sQuery(id+"F4.wireOp",EDGE,"E7.1.1"),sQuery(id+"F4.wireOp",EDGE,"E7.1.2"),sQuery(id+"F4.wireOp",EDGE,"E7.1.4"),sQuery(id+"F4.wireOp",EDGE,"E7.2.0"),sQuery(id+"F4.wireOp",EDGE,"E7.2.1"),subQ1,sQuery(id+"F4.wireOp",EDGE,"E7.2.4"),subQ0,sQuery(id+"F4.wireOp",EDGE,"E9")])],"isStart":false})]});}
            var Q27;
            {var subQ0=sQuery(id+"F4.wireOp",EDGE,"E8");Q27=makeQuery(id+"F5.opExtrude","CAP_EDGE",EDGE,{"disambiguationData":[OSD([subQ0]),TDD([makeQuery(id+"F4.imprint","IMPRINT",EDGE,{"disambiguationData":[TD([[makeQuery(id+"F4.imprint","INTERSECT",VERTEX,{"derivedFrom":[sQuery(id+"F4.wireOp",EDGE,"E7.1.4"),subQ0]}),-1.0]])],"derivedFrom":subQ0})])],"isStart":false});}
            var Q28;
            {var subQ0=sQuery(id+"F4.wireOp",EDGE,"E8");var subQ1=sQuery(id+"F4.wireOp",EDGE,"E7.1.4");Q28=makeQuery(id+"F6.opFillet","BLEND_EDGE",EDGE,{"blendedFrom":[makeQuery(id+"F5.opExtrude","SWEPT_EDGE",EDGE,{"disambiguationData":[OSD([subQ1,subQ0])]}),makeQuery(id+"F5.opExtrude","CAP_FACE",FACE,{"disambiguationData":[OSD([sQuery(id+"F4.wireOp",EDGE,"E5.0"),sQuery(id+"F4.wireOp",EDGE,"E6.0"),sQuery(id+"F4.wireOp",EDGE,"gArRicI1-MkRc-wUEB-PXOf-4bWENSXwJS3J"),sQuery(id+"F4.wireOp",EDGE,"8a5024f6-34da-4b4a-a497-6fec5d8cf57b0.MirrorCS"),sQuery(id+"F4.wireOp",EDGE,"E7.1.0"),sQuery(id+"F4.wireOp",EDGE,"E7.1.1"),sQuery(id+"F4.wireOp",EDGE,"E7.1.2"),subQ1,sQuery(id+"F4.wireOp",EDGE,"E7.2.0"),sQuery(id+"F4.wireOp",EDGE,"E7.2.1"),sQuery(id+"F4.wireOp",EDGE,"E7.2.2"),sQuery(id+"F4.wireOp",EDGE,"E7.2.4"),subQ0,sQuery(id+"F4.wireOp",EDGE,"E9")])],"isStart":false})],"blendedInto":[makeQuery(id+"F5.opExtrude","CAP_FACE",FACE,{"disambiguationData":[OSD([sQuery(id+"F4.wireOp",EDGE,"E5.0"),sQuery(id+"F4.wireOp",EDGE,"E6.0"),sQuery(id+"F4.wireOp",EDGE,"gArRicI1-MkRc-wUEB-PXOf-4bWENSXwJS3J"),sQuery(id+"F4.wireOp",EDGE,"8a5024f6-34da-4b4a-a497-6fec5d8cf57b0.MirrorCS"),sQuery(id+"F4.wireOp",EDGE,"E7.1.0"),sQuery(id+"F4.wireOp",EDGE,"E7.1.1"),sQuery(id+"F4.wireOp",EDGE,"E7.1.2"),subQ1,sQuery(id+"F4.wireOp",EDGE,"E7.2.0"),sQuery(id+"F4.wireOp",EDGE,"E7.2.1"),sQuery(id+"F4.wireOp",EDGE,"E7.2.2"),sQuery(id+"F4.wireOp",EDGE,"E7.2.4"),subQ0,sQuery(id+"F4.wireOp",EDGE,"E9")])],"isStart":false})]});}
            var Q29;
            Q29=makeQuery(id+"F5.opExtrude","CAP_EDGE",EDGE,{"disambiguationData":[OSD([sQuery(id+"F4.wireOp",EDGE,"E7.1.4")])],"isStart":false});
            var Q30;
            {var subQ0=sQuery(id+"F4.wireOp",EDGE,"E7.1.4");var subQ1=sQuery(id+"F4.wireOp",EDGE,"E7.1.0");Q30=makeQuery(id+"F6.opFillet","BLEND_EDGE",EDGE,{"blendedFrom":[makeQuery(id+"F5.opExtrude","SWEPT_EDGE",EDGE,{"disambiguationData":[OSD([subQ1,subQ0])]}),makeQuery(id+"F5.opExtrude","CAP_FACE",FACE,{"disambiguationData":[OSD([sQuery(id+"F4.wireOp",EDGE,"E5.0"),sQuery(id+"F4.wireOp",EDGE,"E6.0"),sQuery(id+"F4.wireOp",EDGE,"gArRicI1-MkRc-wUEB-PXOf-4bWENSXwJS3J"),sQuery(id+"F4.wireOp",EDGE,"8a5024f6-34da-4b4a-a497-6fec5d8cf57b0.MirrorCS"),subQ1,sQuery(id+"F4.wireOp",EDGE,"E7.1.1"),sQuery(id+"F4.wireOp",EDGE,"E7.1.2"),subQ0,sQuery(id+"F4.wireOp",EDGE,"E7.2.0"),sQuery(id+"F4.wireOp",EDGE,"E7.2.1"),sQuery(id+"F4.wireOp",EDGE,"E7.2.2"),sQuery(id+"F4.wireOp",EDGE,"E7.2.4"),sQuery(id+"F4.wireOp",EDGE,"E8"),sQuery(id+"F4.wireOp",EDGE,"E9")])],"isStart":false})],"blendedInto":[makeQuery(id+"F5.opExtrude","CAP_FACE",FACE,{"disambiguationData":[OSD([sQuery(id+"F4.wireOp",EDGE,"E5.0"),sQuery(id+"F4.wireOp",EDGE,"E6.0"),sQuery(id+"F4.wireOp",EDGE,"gArRicI1-MkRc-wUEB-PXOf-4bWENSXwJS3J"),sQuery(id+"F4.wireOp",EDGE,"8a5024f6-34da-4b4a-a497-6fec5d8cf57b0.MirrorCS"),subQ1,sQuery(id+"F4.wireOp",EDGE,"E7.1.1"),sQuery(id+"F4.wireOp",EDGE,"E7.1.2"),subQ0,sQuery(id+"F4.wireOp",EDGE,"E7.2.0"),sQuery(id+"F4.wireOp",EDGE,"E7.2.1"),sQuery(id+"F4.wireOp",EDGE,"E7.2.2"),sQuery(id+"F4.wireOp",EDGE,"E7.2.4"),sQuery(id+"F4.wireOp",EDGE,"E8"),sQuery(id+"F4.wireOp",EDGE,"E9")])],"isStart":false})]});}
            var Q31;
            Q31=makeQuery(id+"F5.opExtrude","CAP_EDGE",EDGE,{"disambiguationData":[OSD([sQuery(id+"F4.wireOp",EDGE,"E7.1.0")])],"isStart":false});
            var Q32;
            Q32=makeQuery(id+"F5.opExtrude","CAP_EDGE",EDGE,{"disambiguationData":[OSD([sQuery(id+"F4.wireOp",EDGE,"E7.2.0")])],"isStart":false});
            var Q33;
            {var subQ0=sQuery(id+"F4.wireOp",EDGE,"E7.2.4");var subQ1=sQuery(id+"F4.wireOp",EDGE,"E7.2.0");Q33=makeQuery(id+"F6.opFillet","BLEND_EDGE",EDGE,{"blendedFrom":[makeQuery(id+"F5.opExtrude","SWEPT_EDGE",EDGE,{"disambiguationData":[OSD([subQ1,subQ0])]}),makeQuery(id+"F5.opExtrude","CAP_FACE",FACE,{"disambiguationData":[OSD([sQuery(id+"F4.wireOp",EDGE,"E5.0"),sQuery(id+"F4.wireOp",EDGE,"E6.0"),sQuery(id+"F4.wireOp",EDGE,"gArRicI1-MkRc-wUEB-PXOf-4bWENSXwJS3J"),sQuery(id+"F4.wireOp",EDGE,"8a5024f6-34da-4b4a-a497-6fec5d8cf57b0.MirrorCS"),sQuery(id+"F4.wireOp",EDGE,"E7.1.0"),sQuery(id+"F4.wireOp",EDGE,"E7.1.1"),sQuery(id+"F4.wireOp",EDGE,"E7.1.2"),sQuery(id+"F4.wireOp",EDGE,"E7.1.4"),subQ1,sQuery(id+"F4.wireOp",EDGE,"E7.2.1"),sQuery(id+"F4.wireOp",EDGE,"E7.2.2"),subQ0,sQuery(id+"F4.wireOp",EDGE,"E8"),sQuery(id+"F4.wireOp",EDGE,"E9")])],"isStart":false})],"blendedInto":[makeQuery(id+"F5.opExtrude","CAP_FACE",FACE,{"disambiguationData":[OSD([sQuery(id+"F4.wireOp",EDGE,"E5.0"),sQuery(id+"F4.wireOp",EDGE,"E6.0"),sQuery(id+"F4.wireOp",EDGE,"gArRicI1-MkRc-wUEB-PXOf-4bWENSXwJS3J"),sQuery(id+"F4.wireOp",EDGE,"8a5024f6-34da-4b4a-a497-6fec5d8cf57b0.MirrorCS"),sQuery(id+"F4.wireOp",EDGE,"E7.1.0"),sQuery(id+"F4.wireOp",EDGE,"E7.1.1"),sQuery(id+"F4.wireOp",EDGE,"E7.1.2"),sQuery(id+"F4.wireOp",EDGE,"E7.1.4"),subQ1,sQuery(id+"F4.wireOp",EDGE,"E7.2.1"),sQuery(id+"F4.wireOp",EDGE,"E7.2.2"),subQ0,sQuery(id+"F4.wireOp",EDGE,"E8"),sQuery(id+"F4.wireOp",EDGE,"E9")])],"isStart":false})]});}
            var Q34;
            Q34=makeQuery(id+"F5.opExtrude","CAP_EDGE",EDGE,{"disambiguationData":[OSD([sQuery(id+"F4.wireOp",EDGE,"E7.2.4")])],"isStart":false});
            var Q35;
            {var subQ0=sQuery(id+"F4.wireOp",EDGE,"E8");var subQ1=sQuery(id+"F4.wireOp",EDGE,"E7.2.4");Q35=makeQuery(id+"F6.opFillet","BLEND_EDGE",EDGE,{"blendedFrom":[makeQuery(id+"F5.opExtrude","SWEPT_EDGE",EDGE,{"disambiguationData":[OSD([subQ1,subQ0])]}),makeQuery(id+"F5.opExtrude","CAP_FACE",FACE,{"disambiguationData":[OSD([sQuery(id+"F4.wireOp",EDGE,"E5.0"),sQuery(id+"F4.wireOp",EDGE,"E6.0"),sQuery(id+"F4.wireOp",EDGE,"gArRicI1-MkRc-wUEB-PXOf-4bWENSXwJS3J"),sQuery(id+"F4.wireOp",EDGE,"8a5024f6-34da-4b4a-a497-6fec5d8cf57b0.MirrorCS"),sQuery(id+"F4.wireOp",EDGE,"E7.1.0"),sQuery(id+"F4.wireOp",EDGE,"E7.1.1"),sQuery(id+"F4.wireOp",EDGE,"E7.1.2"),sQuery(id+"F4.wireOp",EDGE,"E7.1.4"),sQuery(id+"F4.wireOp",EDGE,"E7.2.0"),sQuery(id+"F4.wireOp",EDGE,"E7.2.1"),sQuery(id+"F4.wireOp",EDGE,"E7.2.2"),subQ1,subQ0,sQuery(id+"F4.wireOp",EDGE,"E9")])],"isStart":false})],"blendedInto":[makeQuery(id+"F5.opExtrude","CAP_FACE",FACE,{"disambiguationData":[OSD([sQuery(id+"F4.wireOp",EDGE,"E5.0"),sQuery(id+"F4.wireOp",EDGE,"E6.0"),sQuery(id+"F4.wireOp",EDGE,"gArRicI1-MkRc-wUEB-PXOf-4bWENSXwJS3J"),sQuery(id+"F4.wireOp",EDGE,"8a5024f6-34da-4b4a-a497-6fec5d8cf57b0.MirrorCS"),sQuery(id+"F4.wireOp",EDGE,"E7.1.0"),sQuery(id+"F4.wireOp",EDGE,"E7.1.1"),sQuery(id+"F4.wireOp",EDGE,"E7.1.2"),sQuery(id+"F4.wireOp",EDGE,"E7.1.4"),sQuery(id+"F4.wireOp",EDGE,"E7.2.0"),sQuery(id+"F4.wireOp",EDGE,"E7.2.1"),sQuery(id+"F4.wireOp",EDGE,"E7.2.2"),subQ1,subQ0,sQuery(id+"F4.wireOp",EDGE,"E9")])],"isStart":false})]});}
            var Q36;
            {var subQ0=sQuery(id+"F4.wireOp",EDGE,"E8");Q36=makeQuery(id+"F5.opExtrude","CAP_EDGE",EDGE,{"disambiguationData":[OSD([subQ0]),TDD([makeQuery(id+"F4.imprint","IMPRINT",EDGE,{"disambiguationData":[TD([[makeQuery(id+"F4.imprint","INTERSECT",VERTEX,{"derivedFrom":[sQuery(id+"F4.wireOp",EDGE,"gArRicI1-MkRc-wUEB-PXOf-4bWENSXwJS3J"),subQ0]}),1.0]])],"derivedFrom":subQ0})])],"isStart":false});}
            var Q37;
            {var subQ0=sQuery(id+"F4.wireOp",EDGE,"E8");var subQ1=sQuery(id+"F4.wireOp",EDGE,"gArRicI1-MkRc-wUEB-PXOf-4bWENSXwJS3J");Q37=makeQuery(id+"F6.opFillet","BLEND_EDGE",EDGE,{"blendedFrom":[makeQuery(id+"F5.opExtrude","SWEPT_EDGE",EDGE,{"disambiguationData":[OSD([subQ1,subQ0])]}),makeQuery(id+"F5.opExtrude","CAP_FACE",FACE,{"disambiguationData":[OSD([sQuery(id+"F4.wireOp",EDGE,"E5.0"),sQuery(id+"F4.wireOp",EDGE,"E6.0"),subQ1,sQuery(id+"F4.wireOp",EDGE,"8a5024f6-34da-4b4a-a497-6fec5d8cf57b0.MirrorCS"),sQuery(id+"F4.wireOp",EDGE,"E7.1.0"),sQuery(id+"F4.wireOp",EDGE,"E7.1.1"),sQuery(id+"F4.wireOp",EDGE,"E7.1.2"),sQuery(id+"F4.wireOp",EDGE,"E7.1.4"),sQuery(id+"F4.wireOp",EDGE,"E7.2.0"),sQuery(id+"F4.wireOp",EDGE,"E7.2.1"),sQuery(id+"F4.wireOp",EDGE,"E7.2.2"),sQuery(id+"F4.wireOp",EDGE,"E7.2.4"),subQ0,sQuery(id+"F4.wireOp",EDGE,"E9")])],"isStart":false})],"blendedInto":[makeQuery(id+"F5.opExtrude","CAP_FACE",FACE,{"disambiguationData":[OSD([sQuery(id+"F4.wireOp",EDGE,"E5.0"),sQuery(id+"F4.wireOp",EDGE,"E6.0"),subQ1,sQuery(id+"F4.wireOp",EDGE,"8a5024f6-34da-4b4a-a497-6fec5d8cf57b0.MirrorCS"),sQuery(id+"F4.wireOp",EDGE,"E7.1.0"),sQuery(id+"F4.wireOp",EDGE,"E7.1.1"),sQuery(id+"F4.wireOp",EDGE,"E7.1.2"),sQuery(id+"F4.wireOp",EDGE,"E7.1.4"),sQuery(id+"F4.wireOp",EDGE,"E7.2.0"),sQuery(id+"F4.wireOp",EDGE,"E7.2.1"),sQuery(id+"F4.wireOp",EDGE,"E7.2.2"),sQuery(id+"F4.wireOp",EDGE,"E7.2.4"),subQ0,sQuery(id+"F4.wireOp",EDGE,"E9")])],"isStart":false})]});}
            var Q38;
            Q38=makeQuery(id+"F5.opExtrude","CAP_EDGE",EDGE,{"disambiguationData":[OSD([sQuery(id+"F4.wireOp",EDGE,"gArRicI1-MkRc-wUEB-PXOf-4bWENSXwJS3J")])],"isStart":false});
            var Q39;
            {var subQ0=sQuery(id+"F4.wireOp",EDGE,"gArRicI1-MkRc-wUEB-PXOf-4bWENSXwJS3J");var subQ1=sQuery(id+"F4.wireOp",EDGE,"E6.0");Q39=makeQuery(id+"F6.opFillet","BLEND_EDGE",EDGE,{"blendedFrom":[makeQuery(id+"F5.opExtrude","SWEPT_EDGE",EDGE,{"disambiguationData":[OSD([subQ1,subQ0])]}),makeQuery(id+"F5.opExtrude","CAP_FACE",FACE,{"disambiguationData":[OSD([sQuery(id+"F4.wireOp",EDGE,"E5.0"),subQ1,subQ0,sQuery(id+"F4.wireOp",EDGE,"8a5024f6-34da-4b4a-a497-6fec5d8cf57b0.MirrorCS"),sQuery(id+"F4.wireOp",EDGE,"E7.1.0"),sQuery(id+"F4.wireOp",EDGE,"E7.1.1"),sQuery(id+"F4.wireOp",EDGE,"E7.1.2"),sQuery(id+"F4.wireOp",EDGE,"E7.1.4"),sQuery(id+"F4.wireOp",EDGE,"E7.2.0"),sQuery(id+"F4.wireOp",EDGE,"E7.2.1"),sQuery(id+"F4.wireOp",EDGE,"E7.2.2"),sQuery(id+"F4.wireOp",EDGE,"E7.2.4"),sQuery(id+"F4.wireOp",EDGE,"E8"),sQuery(id+"F4.wireOp",EDGE,"E9")])],"isStart":false})],"blendedInto":[makeQuery(id+"F5.opExtrude","CAP_FACE",FACE,{"disambiguationData":[OSD([sQuery(id+"F4.wireOp",EDGE,"E5.0"),subQ1,subQ0,sQuery(id+"F4.wireOp",EDGE,"8a5024f6-34da-4b4a-a497-6fec5d8cf57b0.MirrorCS"),sQuery(id+"F4.wireOp",EDGE,"E7.1.0"),sQuery(id+"F4.wireOp",EDGE,"E7.1.1"),sQuery(id+"F4.wireOp",EDGE,"E7.1.2"),sQuery(id+"F4.wireOp",EDGE,"E7.1.4"),sQuery(id+"F4.wireOp",EDGE,"E7.2.0"),sQuery(id+"F4.wireOp",EDGE,"E7.2.1"),sQuery(id+"F4.wireOp",EDGE,"E7.2.2"),sQuery(id+"F4.wireOp",EDGE,"E7.2.4"),sQuery(id+"F4.wireOp",EDGE,"E8"),sQuery(id+"F4.wireOp",EDGE,"E9")])],"isStart":false})]});}
            var Q40;
            Q40=makeQuery(id+"F5.opExtrude","CAP_EDGE",EDGE,{"disambiguationData":[OSD([sQuery(id+"F4.wireOp",EDGE,"E6.0")])],"isStart":false});
            var Q41;
            {var subQ0=sQuery(id+"F4.wireOp",EDGE,"8a5024f6-34da-4b4a-a497-6fec5d8cf57b0.MirrorCS");var subQ1=sQuery(id+"F4.wireOp",EDGE,"E6.0");Q41=makeQuery(id+"F6.opFillet","BLEND_EDGE",EDGE,{"blendedFrom":[makeQuery(id+"F5.opExtrude","SWEPT_EDGE",EDGE,{"disambiguationData":[OSD([subQ1,subQ0])]}),makeQuery(id+"F5.opExtrude","CAP_FACE",FACE,{"disambiguationData":[OSD([sQuery(id+"F4.wireOp",EDGE,"E5.0"),subQ1,sQuery(id+"F4.wireOp",EDGE,"gArRicI1-MkRc-wUEB-PXOf-4bWENSXwJS3J"),subQ0,sQuery(id+"F4.wireOp",EDGE,"E7.1.0"),sQuery(id+"F4.wireOp",EDGE,"E7.1.1"),sQuery(id+"F4.wireOp",EDGE,"E7.1.2"),sQuery(id+"F4.wireOp",EDGE,"E7.1.4"),sQuery(id+"F4.wireOp",EDGE,"E7.2.0"),sQuery(id+"F4.wireOp",EDGE,"E7.2.1"),sQuery(id+"F4.wireOp",EDGE,"E7.2.2"),sQuery(id+"F4.wireOp",EDGE,"E7.2.4"),sQuery(id+"F4.wireOp",EDGE,"E8"),sQuery(id+"F4.wireOp",EDGE,"E9")])],"isStart":false})],"blendedInto":[makeQuery(id+"F5.opExtrude","CAP_FACE",FACE,{"disambiguationData":[OSD([sQuery(id+"F4.wireOp",EDGE,"E5.0"),subQ1,sQuery(id+"F4.wireOp",EDGE,"gArRicI1-MkRc-wUEB-PXOf-4bWENSXwJS3J"),subQ0,sQuery(id+"F4.wireOp",EDGE,"E7.1.0"),sQuery(id+"F4.wireOp",EDGE,"E7.1.1"),sQuery(id+"F4.wireOp",EDGE,"E7.1.2"),sQuery(id+"F4.wireOp",EDGE,"E7.1.4"),sQuery(id+"F4.wireOp",EDGE,"E7.2.0"),sQuery(id+"F4.wireOp",EDGE,"E7.2.1"),sQuery(id+"F4.wireOp",EDGE,"E7.2.2"),sQuery(id+"F4.wireOp",EDGE,"E7.2.4"),sQuery(id+"F4.wireOp",EDGE,"E8"),sQuery(id+"F4.wireOp",EDGE,"E9")])],"isStart":false})]});}
            var Q42;
            Q42=makeQuery(id+"F5.opExtrude","CAP_EDGE",EDGE,{"disambiguationData":[OSD([sQuery(id+"F4.wireOp",EDGE,"8a5024f6-34da-4b4a-a497-6fec5d8cf57b0.MirrorCS")])],"isStart":false});
            var Q43;
            {var subQ0=sQuery(id+"F4.wireOp",EDGE,"E8");var subQ1=sQuery(id+"F4.wireOp",EDGE,"8a5024f6-34da-4b4a-a497-6fec5d8cf57b0.MirrorCS");Q43=makeQuery(id+"F6.opFillet","BLEND_EDGE",EDGE,{"blendedFrom":[makeQuery(id+"F5.opExtrude","SWEPT_EDGE",EDGE,{"disambiguationData":[OSD([subQ1,subQ0])]}),makeQuery(id+"F5.opExtrude","CAP_FACE",FACE,{"disambiguationData":[OSD([sQuery(id+"F4.wireOp",EDGE,"E5.0"),sQuery(id+"F4.wireOp",EDGE,"E6.0"),sQuery(id+"F4.wireOp",EDGE,"gArRicI1-MkRc-wUEB-PXOf-4bWENSXwJS3J"),subQ1,sQuery(id+"F4.wireOp",EDGE,"E7.1.0"),sQuery(id+"F4.wireOp",EDGE,"E7.1.1"),sQuery(id+"F4.wireOp",EDGE,"E7.1.2"),sQuery(id+"F4.wireOp",EDGE,"E7.1.4"),sQuery(id+"F4.wireOp",EDGE,"E7.2.0"),sQuery(id+"F4.wireOp",EDGE,"E7.2.1"),sQuery(id+"F4.wireOp",EDGE,"E7.2.2"),sQuery(id+"F4.wireOp",EDGE,"E7.2.4"),subQ0,sQuery(id+"F4.wireOp",EDGE,"E9")])],"isStart":false})],"blendedInto":[makeQuery(id+"F5.opExtrude","CAP_FACE",FACE,{"disambiguationData":[OSD([sQuery(id+"F4.wireOp",EDGE,"E5.0"),sQuery(id+"F4.wireOp",EDGE,"E6.0"),sQuery(id+"F4.wireOp",EDGE,"gArRicI1-MkRc-wUEB-PXOf-4bWENSXwJS3J"),subQ1,sQuery(id+"F4.wireOp",EDGE,"E7.1.0"),sQuery(id+"F4.wireOp",EDGE,"E7.1.1"),sQuery(id+"F4.wireOp",EDGE,"E7.1.2"),sQuery(id+"F4.wireOp",EDGE,"E7.1.4"),sQuery(id+"F4.wireOp",EDGE,"E7.2.0"),sQuery(id+"F4.wireOp",EDGE,"E7.2.1"),sQuery(id+"F4.wireOp",EDGE,"E7.2.2"),sQuery(id+"F4.wireOp",EDGE,"E7.2.4"),subQ0,sQuery(id+"F4.wireOp",EDGE,"E9")])],"isStart":false})]});}
            var Q44;
            {var subQ0=sQuery(id+"F4.wireOp",EDGE,"E8");Q44=makeQuery(id+"F5.opExtrude","CAP_EDGE",EDGE,{"disambiguationData":[OSD([subQ0]),TDD([makeQuery(id+"F4.imprint","IMPRINT",EDGE,{"disambiguationData":[TD([[makeQuery(id+"F4.imprint","INTERSECT",VERTEX,{"derivedFrom":[sQuery(id+"F4.wireOp",EDGE,"8a5024f6-34da-4b4a-a497-6fec5d8cf57b0.MirrorCS"),subQ0]}),-1.0]])],"derivedFrom":subQ0})])],"isStart":false});}
            var Q45;
            {var subQ0=sQuery(id+"F4.wireOp",EDGE,"E8");var subQ1=sQuery(id+"F4.wireOp",EDGE,"E7.1.2");Q45=makeQuery(id+"F6.opFillet","BLEND_EDGE",EDGE,{"blendedFrom":[makeQuery(id+"F5.opExtrude","SWEPT_EDGE",EDGE,{"disambiguationData":[OSD([subQ1,subQ0])]}),makeQuery(id+"F5.opExtrude","CAP_FACE",FACE,{"disambiguationData":[OSD([sQuery(id+"F4.wireOp",EDGE,"E5.0"),sQuery(id+"F4.wireOp",EDGE,"E6.0"),sQuery(id+"F4.wireOp",EDGE,"gArRicI1-MkRc-wUEB-PXOf-4bWENSXwJS3J"),sQuery(id+"F4.wireOp",EDGE,"8a5024f6-34da-4b4a-a497-6fec5d8cf57b0.MirrorCS"),sQuery(id+"F4.wireOp",EDGE,"E7.1.0"),sQuery(id+"F4.wireOp",EDGE,"E7.1.1"),subQ1,sQuery(id+"F4.wireOp",EDGE,"E7.1.4"),sQuery(id+"F4.wireOp",EDGE,"E7.2.0"),sQuery(id+"F4.wireOp",EDGE,"E7.2.1"),sQuery(id+"F4.wireOp",EDGE,"E7.2.2"),sQuery(id+"F4.wireOp",EDGE,"E7.2.4"),subQ0,sQuery(id+"F4.wireOp",EDGE,"E9")])],"isStart":false})],"blendedInto":[makeQuery(id+"F5.opExtrude","CAP_FACE",FACE,{"disambiguationData":[OSD([sQuery(id+"F4.wireOp",EDGE,"E5.0"),sQuery(id+"F4.wireOp",EDGE,"E6.0"),sQuery(id+"F4.wireOp",EDGE,"gArRicI1-MkRc-wUEB-PXOf-4bWENSXwJS3J"),sQuery(id+"F4.wireOp",EDGE,"8a5024f6-34da-4b4a-a497-6fec5d8cf57b0.MirrorCS"),sQuery(id+"F4.wireOp",EDGE,"E7.1.0"),sQuery(id+"F4.wireOp",EDGE,"E7.1.1"),subQ1,sQuery(id+"F4.wireOp",EDGE,"E7.1.4"),sQuery(id+"F4.wireOp",EDGE,"E7.2.0"),sQuery(id+"F4.wireOp",EDGE,"E7.2.1"),sQuery(id+"F4.wireOp",EDGE,"E7.2.2"),sQuery(id+"F4.wireOp",EDGE,"E7.2.4"),subQ0,sQuery(id+"F4.wireOp",EDGE,"E9")])],"isStart":false})]});}
            var Q46;
            Q46=makeQuery(id+"F5.opExtrude","CAP_EDGE",EDGE,{"disambiguationData":[OSD([sQuery(id+"F4.wireOp",EDGE,"E7.1.2")])],"isStart":false});
            var Q47;
            {var subQ0=sQuery(id+"F4.wireOp",EDGE,"E7.1.2");var subQ1=sQuery(id+"F4.wireOp",EDGE,"E7.1.0");Q47=makeQuery(id+"F6.opFillet","BLEND_EDGE",EDGE,{"blendedFrom":[makeQuery(id+"F5.opExtrude","SWEPT_EDGE",EDGE,{"disambiguationData":[OSD([subQ1,subQ0])]}),makeQuery(id+"F5.opExtrude","CAP_FACE",FACE,{"disambiguationData":[OSD([sQuery(id+"F4.wireOp",EDGE,"E5.0"),sQuery(id+"F4.wireOp",EDGE,"E6.0"),sQuery(id+"F4.wireOp",EDGE,"gArRicI1-MkRc-wUEB-PXOf-4bWENSXwJS3J"),sQuery(id+"F4.wireOp",EDGE,"8a5024f6-34da-4b4a-a497-6fec5d8cf57b0.MirrorCS"),subQ1,sQuery(id+"F4.wireOp",EDGE,"E7.1.1"),subQ0,sQuery(id+"F4.wireOp",EDGE,"E7.1.4"),sQuery(id+"F4.wireOp",EDGE,"E7.2.0"),sQuery(id+"F4.wireOp",EDGE,"E7.2.1"),sQuery(id+"F4.wireOp",EDGE,"E7.2.2"),sQuery(id+"F4.wireOp",EDGE,"E7.2.4"),sQuery(id+"F4.wireOp",EDGE,"E8"),sQuery(id+"F4.wireOp",EDGE,"E9")])],"isStart":false})],"blendedInto":[makeQuery(id+"F5.opExtrude","CAP_FACE",FACE,{"disambiguationData":[OSD([sQuery(id+"F4.wireOp",EDGE,"E5.0"),sQuery(id+"F4.wireOp",EDGE,"E6.0"),sQuery(id+"F4.wireOp",EDGE,"gArRicI1-MkRc-wUEB-PXOf-4bWENSXwJS3J"),sQuery(id+"F4.wireOp",EDGE,"8a5024f6-34da-4b4a-a497-6fec5d8cf57b0.MirrorCS"),subQ1,sQuery(id+"F4.wireOp",EDGE,"E7.1.1"),subQ0,sQuery(id+"F4.wireOp",EDGE,"E7.1.4"),sQuery(id+"F4.wireOp",EDGE,"E7.2.0"),sQuery(id+"F4.wireOp",EDGE,"E7.2.1"),sQuery(id+"F4.wireOp",EDGE,"E7.2.2"),sQuery(id+"F4.wireOp",EDGE,"E7.2.4"),sQuery(id+"F4.wireOp",EDGE,"E8"),sQuery(id+"F4.wireOp",EDGE,"E9")])],"isStart":false})]});}
            fillet(context, id + "F7", {"entities" : qUnion([Q0, Q1, Q2, Q3, Q4, Q5, Q6, Q7, Q8, Q9, Q10, Q11, Q12, Q13, Q14, Q15, Q16, Q17, Q18, Q19, Q20, Q21, Q22, Q23, Q24, Q25, Q26, Q27, Q28, Q29, Q30, Q31, Q32, Q33, Q34, Q35, Q36, Q37, Q38, Q39, Q40, Q41, Q42, Q43, Q44, Q45, Q46, Q47]), "radius" : 1 * mm, "tangentPropagation" : true, "allowEdgeOverflow" : false});
        }
    });
